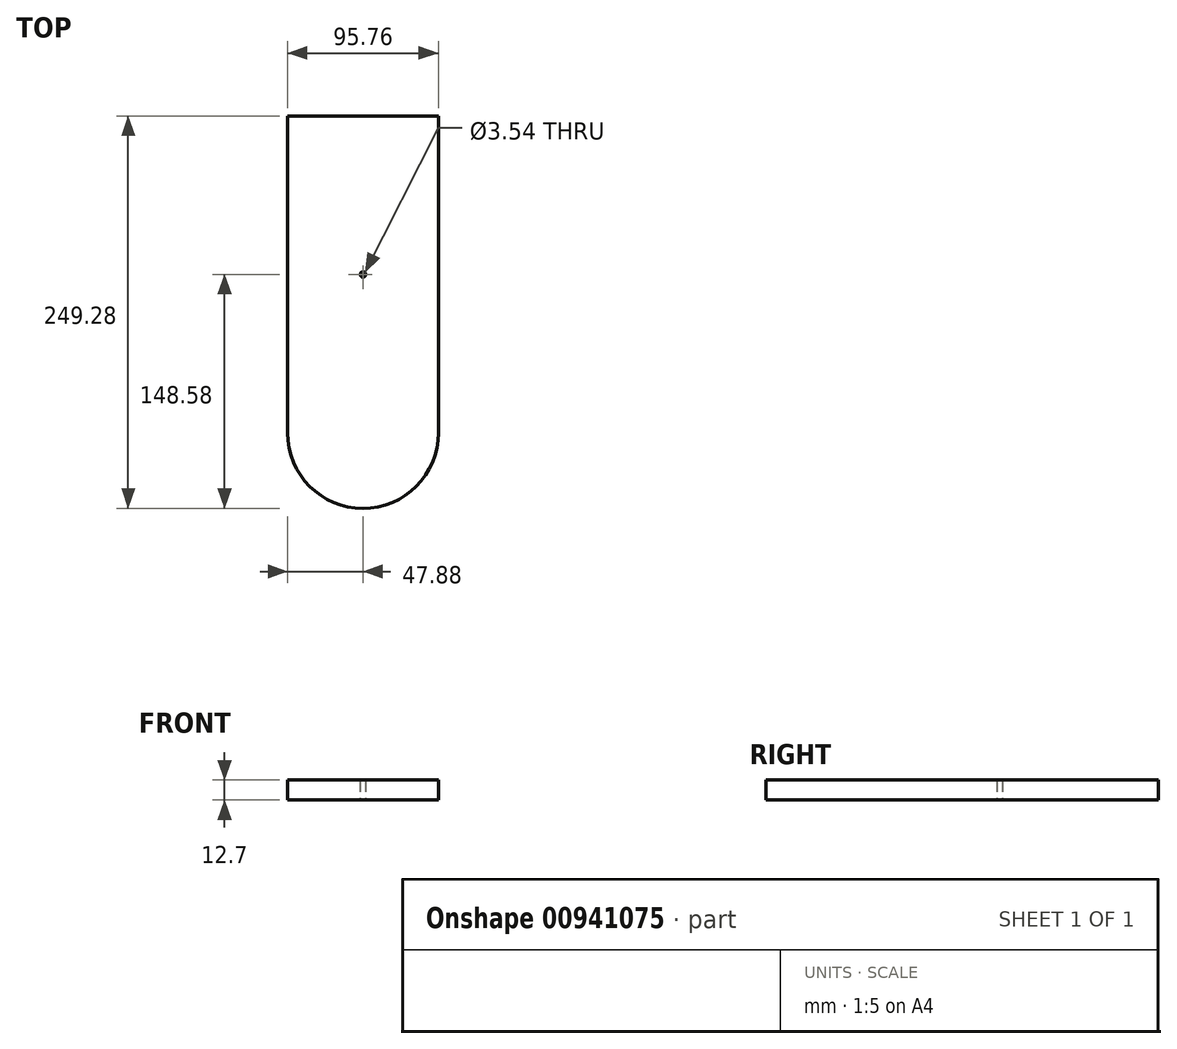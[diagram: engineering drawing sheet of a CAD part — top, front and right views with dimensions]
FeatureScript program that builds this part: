
annotation { "Feature Type Name" : "Feature", "Feature Type Description" : "" }
export const myFeature = defineFeature(function(context is Context, id is Id, definition is map)
    precondition{}
    {
        {
            var Q0;
            Q0=qCreatedBy(makeId("Top.planeOp"),FACE);
            var sketch = newSketch(context, id + "F0", { "sketchPlane" : qUnion([Q0])});
            skLineSegment(sketch, "E0.bottom", {"start": v(-47.88, 100.7) * mm, "end": v(47.88, 100.7) * mm});
            skLineSegment(sketch, "E0.top", {"start": v(-47.88, -100.7) * mm, "end": v(47.88, -100.7) * mm});
            skLineSegment(sketch, "E0.left", {"start": v(-47.88, 100.7) * mm, "end": v(-47.88, -100.7) * mm});
            skLineSegment(sketch, "E0.right", {"start": v(47.88, 100.7) * mm, "end": v(47.88, -100.7) * mm});
            skPoint(sketch, "E0.middle", {"position": v(0, 0) * mm});
            skArc(sketch, "E1", {"start": v(-47.88, -100.7) * mm, "mid": v(0, -148.58) * mm, "end": v(47.88, -100.7) * mm});
            skLineSegment(sketch, "E2.bottom", {"start": v(-47.88, 20.58) * mm, "end": v(0, 20.58) * mm});
            skLineSegment(sketch, "E2.top", {"start": v(-47.88, 53.32) * mm, "end": v(0, 53.32) * mm});
            skLineSegment(sketch, "E2.left", {"start": v(-47.88, 20.58) * mm, "end": v(-47.88, 53.32) * mm});
            skLineSegment(sketch, "E2.right", {"start": v(0, 20.58) * mm, "end": v(0, 53.32) * mm});
            skCircle(sketch, "E3", {"center": v(0, 0) * mm, "radius": 1.77 * mm});
            skSolve(sketch);
        }
        {
            var Q0;
            Q0 = qSketchRegion(id + "F0", true);
            var Q1;
            Q1=makeQuery(id+"F0.imprint","IMPRINT",FACE,{"disambiguationData":[TD([[makeQuery(id+"F0.imprint","IMPRINT",EDGE,{"derivedFrom":sQuery(id+"F0.wireOp",EDGE,"E2.bottom")}),1.0]])]});
            var Q2;
            Q2=makeQuery(id+"F0.imprint","IMPRINT",FACE,{"disambiguationData":[TD([[makeQuery(id+"F0.imprint","IMPRINT",EDGE,{"derivedFrom":sQuery(id+"F0.wireOp",EDGE,"E0.top")}),-1.0]])]});
            var Q3;
            {var subQ4=sQuery(id+"F0.wireOp",EDGE,"E0.bottom");Q3=makeQuery(id+"F0.imprint","IMPRINT",FACE,{"disambiguationData":[TD([[makeQuery(id+"F0.imprint","IMPRINT",EDGE,{"derivedFrom":subQ4}),-1.0]])]});}
            extrude(context, id + "F1", {"entities" : qUnion([Q0, Q1, Q2, Q3]), "depth" : 12.7 * mm, "offsetDistance" : 25.4 * mm});
        }
    });
